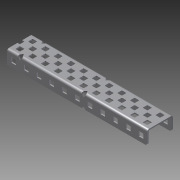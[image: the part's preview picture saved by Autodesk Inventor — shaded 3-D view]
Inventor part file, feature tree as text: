
AUTODESK INVENTOR PART (.ipt)
format: ipt  version: 2014 SP1 (Build 180222100, 222)  size: 936,448 bytes
history: native  units: in
note: dims shown in document units (in); Inventor stores cm internally (conversion verified against a paired STEP export)
features: other x1, imported_body x1, extrude x1, sketch x1
ambient origin geometry x8: Origin, YZ Plane, XZ Plane, XY Plane, X Axis, Y Axis, Z Axis, Center Point
bodies: Body1 (feature_tree)
feature tree (4):
  parser-record x1  (decoder bookkeeping rows leaked as tree rows — omitted from the tree; the rows remain in map.json)
  imported_body  "Base1"
  extrude  "Extrusion1"  Depth=1.0in TaperAngle=0.0deg
  sketch  "Sketch1"  dims[d0=2.0in d1=1.0in d2=0.0in]
